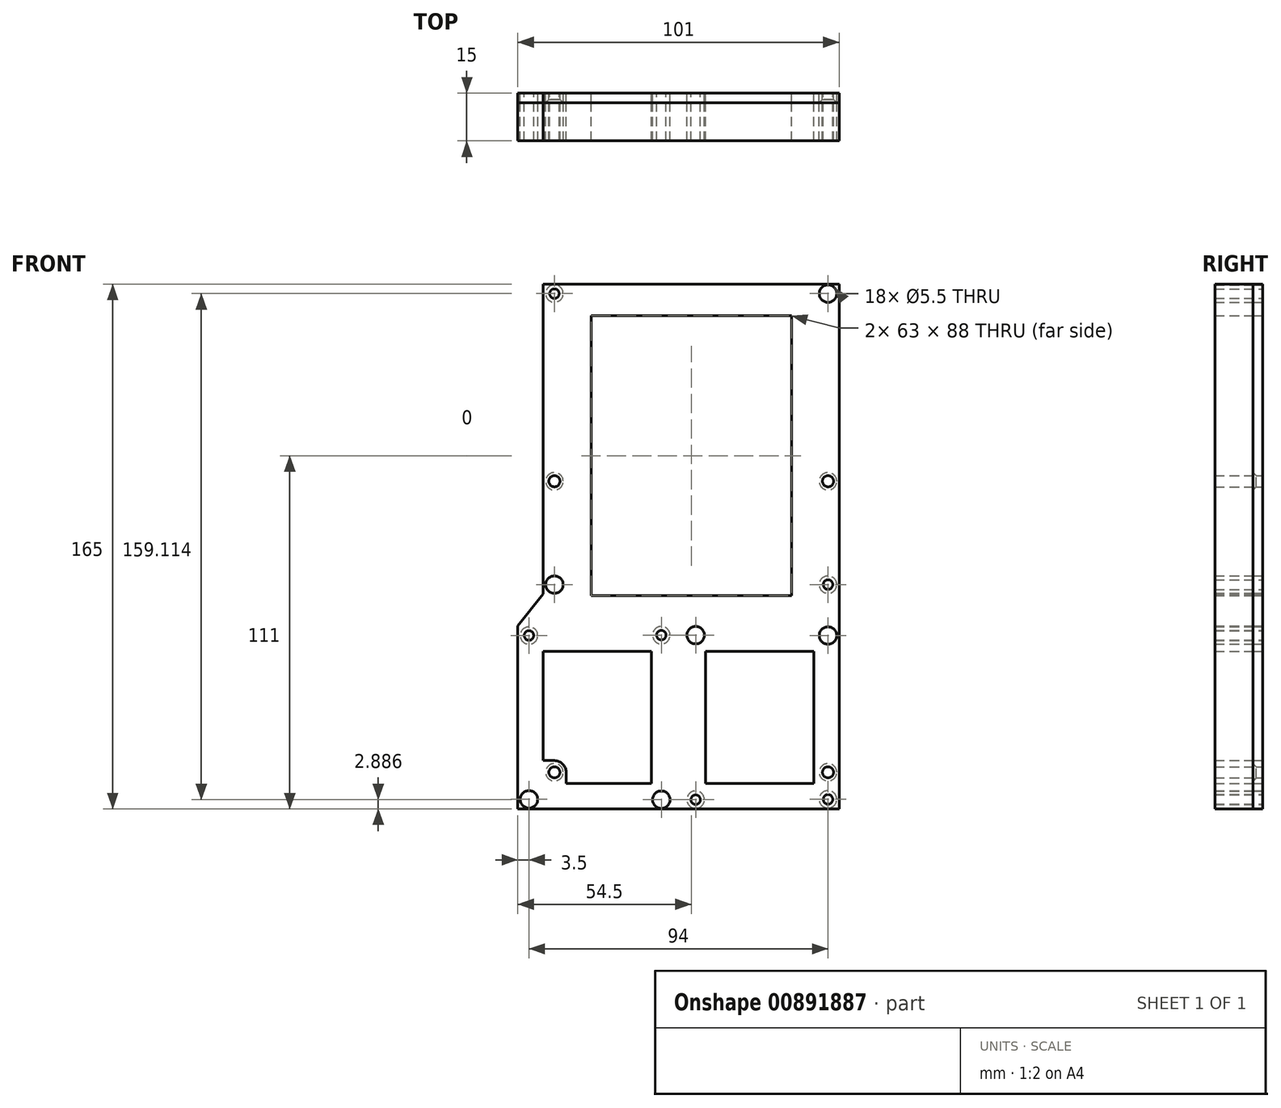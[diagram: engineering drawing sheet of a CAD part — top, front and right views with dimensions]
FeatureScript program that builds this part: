
annotation { "Feature Type Name" : "Feature", "Feature Type Description" : "" }
export const myFeature = defineFeature(function(context is Context, id is Id, definition is map)
    precondition{}
    {
        {
            var Q0;
            Q0=qCreatedBy(makeId("Front.planeOp"),FACE);
            var sketch = newSketch(context, id + "F0", { "sketchPlane" : qUnion([Q0])});
            skLineSegment(sketch, "E0.bottom", {"start": v(-93, 97.5) * mm, "end": v(0, 97.5) * mm});
            skLineSegment(sketch, "E0.top", {"start": v(-93, 0) * mm, "end": v(-89.5, 0) * mm});
            skLineSegment(sketch, "E0.left", {"start": v(-93, 97.5) * mm, "end": v(-93, 0) * mm});
            skLineSegment(sketch, "E0.right", {"start": v(0, 97.5) * mm, "end": v(0, 0) * mm});
            skLineSegment(sketch, "E1.bottom", {"start": v(-78, 87.5) * mm, "end": v(-15, 87.5) * mm});
            skLineSegment(sketch, "E1.top", {"start": v(-78, -0.5) * mm, "end": v(-15, -0.5) * mm});
            skLineSegment(sketch, "E1.left", {"start": v(-78, 87.5) * mm, "end": v(-78, -0.5) * mm});
            skLineSegment(sketch, "E1.right", {"start": v(-15, 87.5) * mm, "end": v(-15, -0.5) * mm});
            skCircle(sketch, "E2", {"center": v(-89.5, 94.5) * mm, "radius": 2.75 * mm});
            skCircle(sketch, "E3", {"center": v(-89.5, 94.5) * mm, "radius": 1.5 * mm});
            skLineSegment(sketch, "E4", {"start": v(-46.5, 97.5) * mm, "end": v(-46.5, -2.32) * mm, "construction": true});
            skLineSegment(sketch, "E5", {"start": v(-93, 48.75) * mm, "end": v(0, 48.75) * mm, "construction": true});
            skCircle(sketch, "E6.MirrorC", {"center": v(-3.5, 94.5) * mm, "radius": 2.75 * mm});
            skCircle(sketch, "E7.MirrorC", {"center": v(-3.5, 94.5) * mm, "radius": 1.5 * mm});
            skCircle(sketch, "E8.MirrorC", {"center": v(-89.5, 3) * mm, "radius": 2.75 * mm});
            skCircle(sketch, "E9.MirrorC", {"center": v(-89.5, 3) * mm, "radius": 1.5 * mm});
            skCircle(sketch, "E10.MirrorC", {"center": v(-3.5, 3) * mm, "radius": 2.75 * mm});
            skCircle(sketch, "E11.MirrorC", {"center": v(-3.5, 3) * mm, "radius": 1.5 * mm});
            skLineSegment(sketch, "E12", {"start": v(-89.5, 94.5) * mm, "end": v(-89.5, 35.5) * mm, "construction": true});
            skCircle(sketch, "E13", {"center": v(-89.5, 35.5) * mm, "radius": 1.75 * mm});
            skCircle(sketch, "E14.MirrorC", {"center": v(-3.5, 35.5) * mm, "radius": 1.75 * mm});
            skLineSegment(sketch, "E15.bottom", {"start": v(0, -10) * mm, "end": v(-101, -10) * mm});
            skLineSegment(sketch, "E15.top", {"start": v(0, -67.5) * mm, "end": v(-101, -67.5) * mm});
            skLineSegment(sketch, "E15.left", {"start": v(0, -10) * mm, "end": v(0, -67.5) * mm});
            skLineSegment(sketch, "E15.right", {"start": v(-101, -10) * mm, "end": v(-101, -67.5) * mm});
            skLineSegment(sketch, "E16", {"start": v(-111.86, -5) * mm, "end": v(23.5, -5) * mm, "construction": true});
            skCircle(sketch, "E17.MirrorC", {"center": v(-3.5, -13) * mm, "radius": 2.75 * mm});
            skCircle(sketch, "E18.MirrorC", {"center": v(-3.5, -13) * mm, "radius": 1.5 * mm});
            skLineSegment(sketch, "E19", {"start": v(8.77, -38.75) * mm, "end": v(-119.23, -38.75) * mm, "construction": true});
            skPoint(sketch, "E19.startSnap0", {"position": v(0, -38.75) * mm});
            skLineSegment(sketch, "E20", {"start": v(-50.5, -10) * mm, "end": v(-50.5, -67.5) * mm, "construction": true});
            skCircle(sketch, "E21.MirrorC", {"center": v(-3.5, -64.5) * mm, "radius": 2.75 * mm});
            skCircle(sketch, "E22.MirrorC", {"center": v(-3.5, -64.5) * mm, "radius": 1.5 * mm});
            skCircle(sketch, "E23.MirrorC", {"center": v(-97.5, -13) * mm, "radius": 2.75 * mm});
            skCircle(sketch, "E24.MirrorC", {"center": v(-97.5, -13) * mm, "radius": 1.5 * mm});
            skCircle(sketch, "E25.MirrorC", {"center": v(-97.5, -64.5) * mm, "radius": 2.75 * mm});
            skCircle(sketch, "E26.MirrorC", {"center": v(-97.5, -64.5) * mm, "radius": 1.5 * mm});
            skCircle(sketch, "E27", {"center": v(-55.9, -12.89) * mm, "radius": 2.75 * mm});
            skCircle(sketch, "E28", {"center": v(-55.9, -12.89) * mm, "radius": 1.5 * mm});
            skCircle(sketch, "E29.MirrorC", {"center": v(-55.9, -64.61) * mm, "radius": 2.75 * mm});
            skCircle(sketch, "E30.MirrorC", {"center": v(-55.9, -64.61) * mm, "radius": 1.5 * mm});
            skCircle(sketch, "E31.MirrorC", {"center": v(-45.1, -12.89) * mm, "radius": 2.75 * mm});
            skCircle(sketch, "E32.MirrorC", {"center": v(-45.1, -12.89) * mm, "radius": 1.5 * mm});
            skCircle(sketch, "E33.MirrorC", {"center": v(-45.1, -64.61) * mm, "radius": 2.75 * mm});
            skCircle(sketch, "E34.MirrorC", {"center": v(-45.1, -64.61) * mm, "radius": 1.5 * mm});
            skLineSegment(sketch, "E35", {"start": v(0, -10) * mm, "end": v(0, 0) * mm});
            skLineSegment(sketch, "E36", {"start": v(-93, 0) * mm, "end": v(-101, -10) * mm});
            skLineSegment(sketch, "E37", {"start": v(-89.5, 35.5) * mm, "end": v(-89.5, -71.3) * mm, "construction": true});
            skLineSegment(sketch, "E38", {"start": v(-105.82, -64.5) * mm, "end": v(8.18, -64.5) * mm, "construction": true});
            skLineSegment(sketch, "E39.bottom", {"start": v(-93, -18) * mm, "end": v(-59, -18) * mm});
            skLineSegment(sketch, "E39.left", {"start": v(-93, -18) * mm, "end": v(-93, -52.32) * mm});
            skLineSegment(sketch, "E39.right", {"start": v(-59, -18) * mm, "end": v(-59, -59.5) * mm});
            skLineSegment(sketch, "E40.MirrorCS", {"start": v(-42, -18) * mm, "end": v(-42, -59.5) * mm});
            skLineSegment(sketch, "E41.MirrorCS", {"start": v(-8, -18) * mm, "end": v(-42, -18) * mm});
            skLineSegment(sketch, "E42.MirrorCS", {"start": v(-8, -18) * mm, "end": v(-8, -59.5) * mm});
            skLineSegment(sketch, "E43.MirrorCS", {"start": v(-8, -59.5) * mm, "end": v(-42, -59.5) * mm});
            skLineSegment(sketch, "E44", {"start": v(-3.5, -13) * mm, "end": v(-3.5, -68.9) * mm, "construction": true});
            skCircle(sketch, "E45", {"center": v(-3.5, -56) * mm, "radius": 1.75 * mm});
            skCircle(sketch, "E46", {"center": v(-89.5, -56) * mm, "radius": 1.75 * mm});
            skArc(sketch, "E47", {"start": v(-89.5, -52.32) * mm, "mid": v(-86.9, -53.4) * mm, "end": v(-85.82, -56) * mm});
            skLineSegment(sketch, "E48", {"start": v(-89.5, -52.32) * mm, "end": v(-93, -52.32) * mm});
            skLineSegment(sketch, "E49", {"start": v(-85.82, -56) * mm, "end": v(-85.82, -59.5) * mm});
            skLineSegment(sketch, "E50", {"start": v(-85.82, -59.5) * mm, "end": v(-59, -59.5) * mm});
            skSolve(sketch);
        }
        {
            var Q0;
            Q0=makeQuery(id+"F0.imprint","IMPRINT",FACE,{"disambiguationData":[TD([[makeQuery(id+"F0.imprint","IMPRINT",EDGE,{"derivedFrom":sQuery(id+"F0.wireOp",EDGE,"E2")}),1.0]])]});
            var Q1;
            Q1=makeQuery(id+"F0.imprint","IMPRINT",FACE,{"disambiguationData":[TD([[makeQuery(id+"F0.imprint","IMPRINT",EDGE,{"derivedFrom":sQuery(id+"F0.wireOp",EDGE,"E6.MirrorC")}),-1.0]])]});
            var Q2;
            Q2=makeQuery(id+"F0.imprint","IMPRINT",FACE,{"disambiguationData":[TD([[makeQuery(id+"F0.imprint","IMPRINT",EDGE,{"derivedFrom":sQuery(id+"F0.wireOp",EDGE,"E8.MirrorC")}),-1.0]])]});
            var Q3;
            Q3=makeQuery(id+"F0.imprint","IMPRINT",FACE,{"disambiguationData":[TD([[makeQuery(id+"F0.imprint","IMPRINT",EDGE,{"derivedFrom":sQuery(id+"F0.wireOp",EDGE,"E10.MirrorC")}),1.0]])]});
            var Q4;
            Q4=makeQuery(id+"F0.imprint","IMPRINT",FACE,{"disambiguationData":[TD([[makeQuery(id+"F0.imprint","IMPRINT",EDGE,{"derivedFrom":sQuery(id+"F0.wireOp",EDGE,"E17.MirrorC")}),-1.0]])]});
            var Q5;
            Q5=makeQuery(id+"F0.imprint","IMPRINT",FACE,{"disambiguationData":[TD([[makeQuery(id+"F0.imprint","IMPRINT",EDGE,{"derivedFrom":sQuery(id+"F0.wireOp",EDGE,"E31.MirrorC")}),-1.0]])]});
            var Q6;
            Q6=makeQuery(id+"F0.imprint","IMPRINT",FACE,{"disambiguationData":[TD([[makeQuery(id+"F0.imprint","IMPRINT",EDGE,{"derivedFrom":sQuery(id+"F0.wireOp",EDGE,"E27")}),1.0]])]});
            var Q7;
            Q7=makeQuery(id+"F0.imprint","IMPRINT",FACE,{"disambiguationData":[TD([[makeQuery(id+"F0.imprint","IMPRINT",EDGE,{"derivedFrom":sQuery(id+"F0.wireOp",EDGE,"E23.MirrorC")}),1.0]])]});
            var Q8;
            Q8=makeQuery(id+"F0.imprint","IMPRINT",FACE,{"disambiguationData":[TD([[makeQuery(id+"F0.imprint","IMPRINT",EDGE,{"derivedFrom":sQuery(id+"F0.wireOp",EDGE,"E25.MirrorC")}),-1.0]])]});
            var Q9;
            Q9=makeQuery(id+"F0.imprint","IMPRINT",FACE,{"disambiguationData":[TD([[makeQuery(id+"F0.imprint","IMPRINT",EDGE,{"derivedFrom":sQuery(id+"F0.wireOp",EDGE,"E29.MirrorC")}),-1.0]])]});
            var Q10;
            Q10=makeQuery(id+"F0.imprint","IMPRINT",FACE,{"disambiguationData":[TD([[makeQuery(id+"F0.imprint","IMPRINT",EDGE,{"derivedFrom":sQuery(id+"F0.wireOp",EDGE,"E33.MirrorC")}),1.0]])]});
            var Q11;
            Q11=makeQuery(id+"F0.imprint","IMPRINT",FACE,{"disambiguationData":[TD([[makeQuery(id+"F0.imprint","IMPRINT",EDGE,{"derivedFrom":sQuery(id+"F0.wireOp",EDGE,"E21.MirrorC")}),1.0]])]});
            extrude(context, id + "F1", {"entities" : qUnion([Q0, Q1, Q2, Q3, Q4, Q5, Q6, Q7, Q8, Q9, Q10, Q11]), "depth" : 15 * mm, "offsetDistance" : 25 * mm});
        }
        {
            var Q0;
            Q0 = qSketchRegion(id + "F0", true);
            extrude(context, id + "F2", {"entities" : qUnion([Q0]), "depth" : 3 * mm, "offsetDistance" : 25 * mm});
        }
        {
            var Q0;
            Q0=makeQuery(id+"F2.opExtrude","CAP_EDGE",EDGE,{"disambiguationData":[OSD([sQuery(id+"F0.wireOp",EDGE,"E13")])],"isStart":false});
            var Q1;
            Q1=makeQuery(id+"F2.opExtrude","CAP_EDGE",EDGE,{"disambiguationData":[OSD([sQuery(id+"F0.wireOp",EDGE,"E14.MirrorC")])],"isStart":false});
            var Q2;
            Q2=makeQuery(id+"F2.opExtrude","CAP_EDGE",EDGE,{"disambiguationData":[OSD([sQuery(id+"F0.wireOp",EDGE,"E45")])],"isStart":false});
            var Q3;
            Q3=makeQuery(id+"F2.opExtrude","CAP_EDGE",EDGE,{"disambiguationData":[OSD([sQuery(id+"F0.wireOp",EDGE,"E46")])],"isStart":false});
            chamfer(context, id + "F3", {"entities" : qUnion([Q0, Q1, Q2, Q3]), "width" : 1 * mm, "tangentPropagation" : true});
        }
    });
